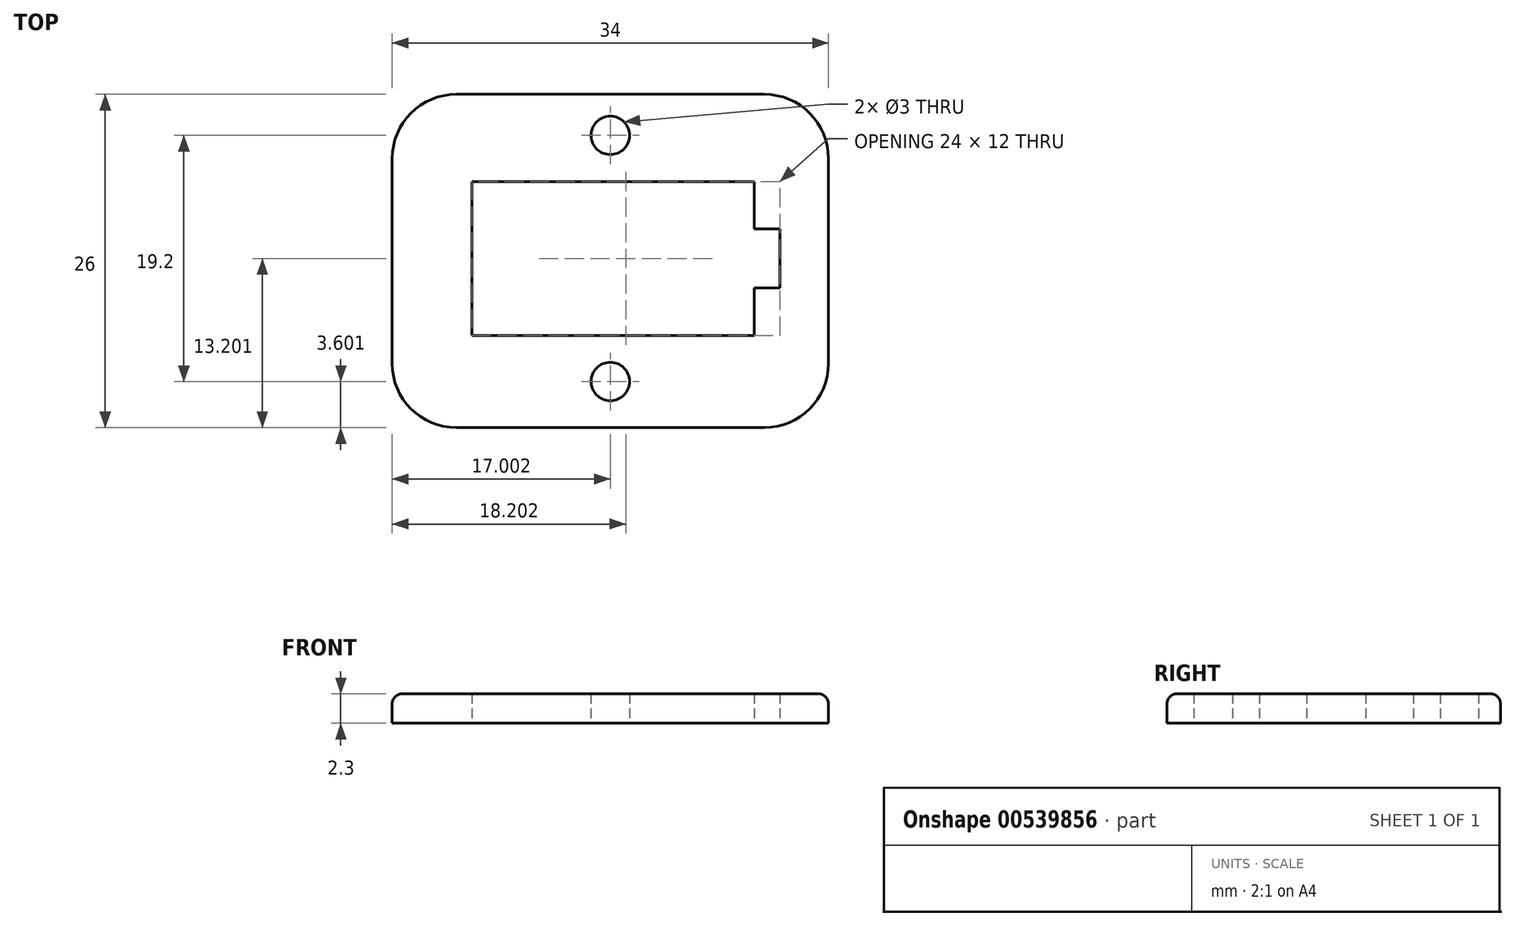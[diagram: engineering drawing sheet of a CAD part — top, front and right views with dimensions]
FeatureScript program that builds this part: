
annotation { "Feature Type Name" : "Feature", "Feature Type Description" : "" }
export const myFeature = defineFeature(function(context is Context, id is Id, definition is map)
    precondition{}
    {
        {
            var Q0;
            Q0=qCreatedBy(makeId("Top.planeOp"),FACE);
            var sketch = newSketch(context, id + "F0", { "sketchPlane" : qUnion([Q0])});
            skLineSegment(sketch, "E0.bottom", {"start": v(-20.13, 14.05) * mm, "end": v(3.87, 14.05) * mm});
            skLineSegment(sketch, "E0.top", {"start": v(-20.13, -11.95) * mm, "end": v(3.87, -11.95) * mm});
            skLineSegment(sketch, "E0.left", {"start": v(-25.13, 9.05) * mm, "end": v(-25.13, -6.95) * mm});
            skLineSegment(sketch, "E0.right", {"start": v(8.87, 9.05) * mm, "end": v(8.87, -6.95) * mm});
            skPoint(sketch, "E1.visualSharp", {"position": v(-25.13, 14.05) * mm});
            skArc(sketch, "E1.filletArc", {"start": v(-20.13, 14.05) * mm, "mid": v(-23.66, 12.59) * mm, "end": v(-25.13, 9.05) * mm});
            skPoint(sketch, "E2.visualSharp", {"position": v(8.87, 14.05) * mm});
            skArc(sketch, "E2.filletArc", {"start": v(8.87, 9.05) * mm, "mid": v(7.4, 12.59) * mm, "end": v(3.87, 14.05) * mm});
            skPoint(sketch, "E3.visualSharp", {"position": v(8.87, -11.95) * mm});
            skArc(sketch, "E3.filletArc", {"start": v(3.87, -11.95) * mm, "mid": v(7.4, -10.48) * mm, "end": v(8.87, -6.95) * mm});
            skPoint(sketch, "E4.visualSharp", {"position": v(-25.13, -11.95) * mm});
            skArc(sketch, "E4.filletArc", {"start": v(-25.13, -6.95) * mm, "mid": v(-23.66, -10.48) * mm, "end": v(-20.13, -11.95) * mm});
            skLineSegment(sketch, "E5", {"start": v(-18.93, -4.75) * mm, "end": v(-18.93, 7.25) * mm});
            skLineSegment(sketch, "E6", {"start": v(-18.93, 7.25) * mm, "end": v(3.07, 7.25) * mm});
            skLineSegment(sketch, "E7", {"start": v(3.07, 7.25) * mm, "end": v(3.07, -4.75) * mm});
            skLineSegment(sketch, "E8", {"start": v(3.07, -4.75) * mm, "end": v(-18.93, -4.75) * mm});
            skLineSegment(sketch, "E9", {"start": v(5.07, 1.25) * mm, "end": v(5.07, -1.05) * mm});
            skLineSegment(sketch, "E10", {"start": v(5.07, 1.25) * mm, "end": v(5.07, 3.55) * mm});
            skLineSegment(sketch, "E11", {"start": v(5.07, 3.55) * mm, "end": v(3.07, 3.55) * mm});
            skLineSegment(sketch, "E12", {"start": v(5.07, -1.05) * mm, "end": v(3.07, -1.05) * mm});
            skCircle(sketch, "E13", {"center": v(-8.13, -8.35) * mm, "radius": 1.5 * mm});
            skLineSegment(sketch, "E14", {"start": v(5.07, 1.25) * mm, "end": v(-4.05, 1.25) * mm});
            skCircle(sketch, "E15.MirrorC", {"center": v(-8.13, 10.85) * mm, "radius": 1.5 * mm});
            skSolve(sketch);
        }
        {
            var Q0;
            Q0=makeQuery(id+"F0.imprint","IMPRINT",FACE,{"disambiguationData":[TD([[makeQuery(id+"F0.imprint","IMPRINT",EDGE,{"derivedFrom":sQuery(id+"F0.wireOp",EDGE,"E0.bottom")}),-1.0]])]});
            extrude(context, id + "F1", {"entities" : qUnion([Q0]), "depth" : 2.3 * mm, "offsetDistance" : 25 * mm});
        }
        {
            var Q0;
            Q0=makeQuery(id+"F1.opExtrude","CAP_EDGE",EDGE,{"disambiguationData":[OSD([sQuery(id+"F0.wireOp",EDGE,"E4.filletArc")])],"isStart":false});
            fillet(context, id + "F2", {"entities" : qUnion([Q0]), "radius" : 0.8 * mm, "tangentPropagation" : true, "allowEdgeOverflow" : false});
        }
    });
